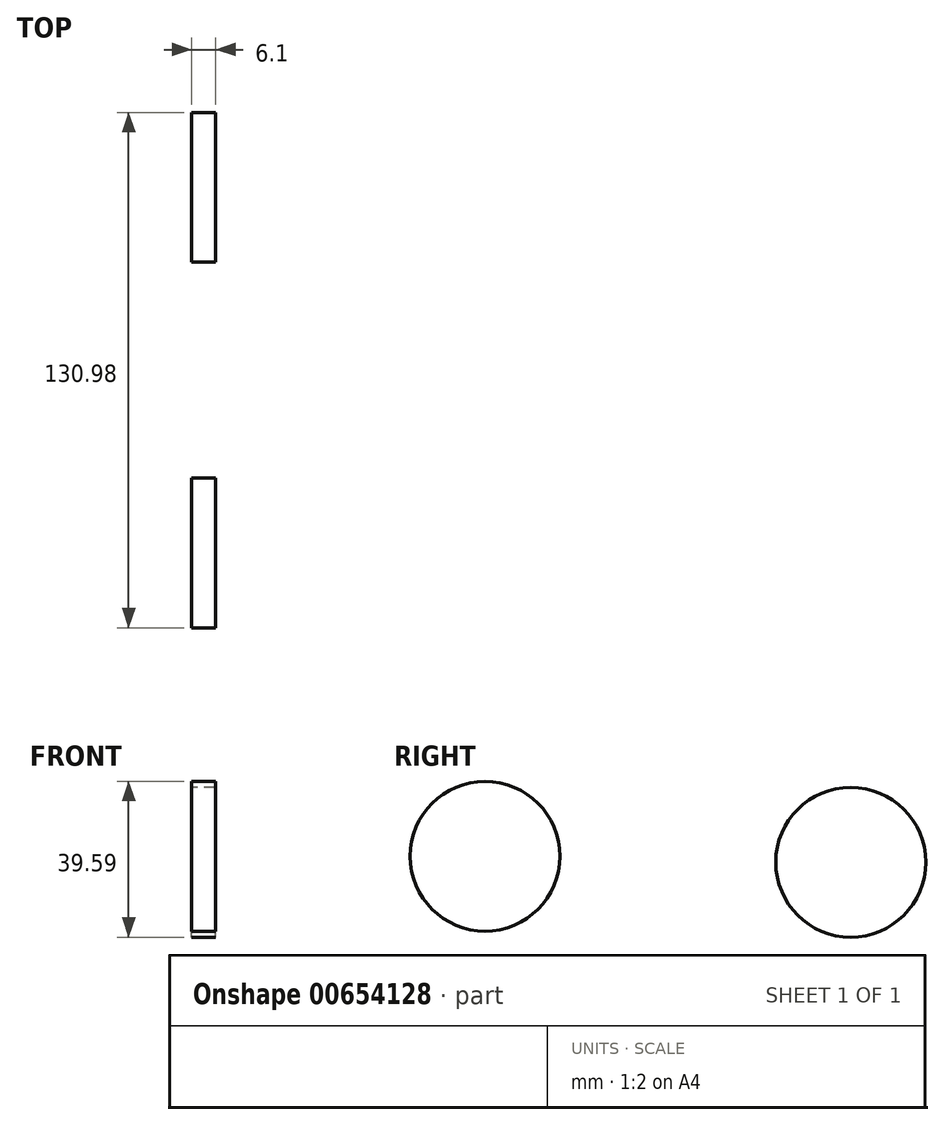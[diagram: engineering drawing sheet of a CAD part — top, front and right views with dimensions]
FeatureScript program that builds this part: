
annotation { "Feature Type Name" : "Feature", "Feature Type Description" : "" }
export const myFeature = defineFeature(function(context is Context, id is Id, definition is map)
    precondition{}
    {
        {
            var Q0;
            Q0=qCreatedBy(makeId("Right.planeOp"),FACE);
            var sketch = newSketch(context, id + "F0", { "sketchPlane" : qUnion([Q0])});
            skCircle(sketch, "E0", {"center": v(43.51, -14.12) * mm, "radius": 19.04 * mm});
            skCircle(sketch, "E1", {"center": v(-49.4, -12.6) * mm, "radius": 19.03 * mm});
            skSolve(sketch);
        }
        {
            var Q0;
            Q0=makeQuery(id+"F0.imprint","IMPRINT",FACE,{"disambiguationData":[TD([[makeQuery(id+"F0.imprint","IMPRINT",EDGE,{"derivedFrom":sQuery(id+"F0.wireOp",EDGE,"E1")}),1.0]])]});
            var Q1;
            Q1=makeQuery(id+"F0.imprint","IMPRINT",FACE,{"disambiguationData":[TD([[makeQuery(id+"F0.imprint","IMPRINT",EDGE,{"derivedFrom":sQuery(id+"F0.wireOp",EDGE,"E0")}),1.0]])]});
            extrude(context, id + "F1", {"entities" : qUnion([Q0, Q1]), "depth" : 6.1 * mm, "offsetDistance" : 25.4 * mm});
        }
    });
